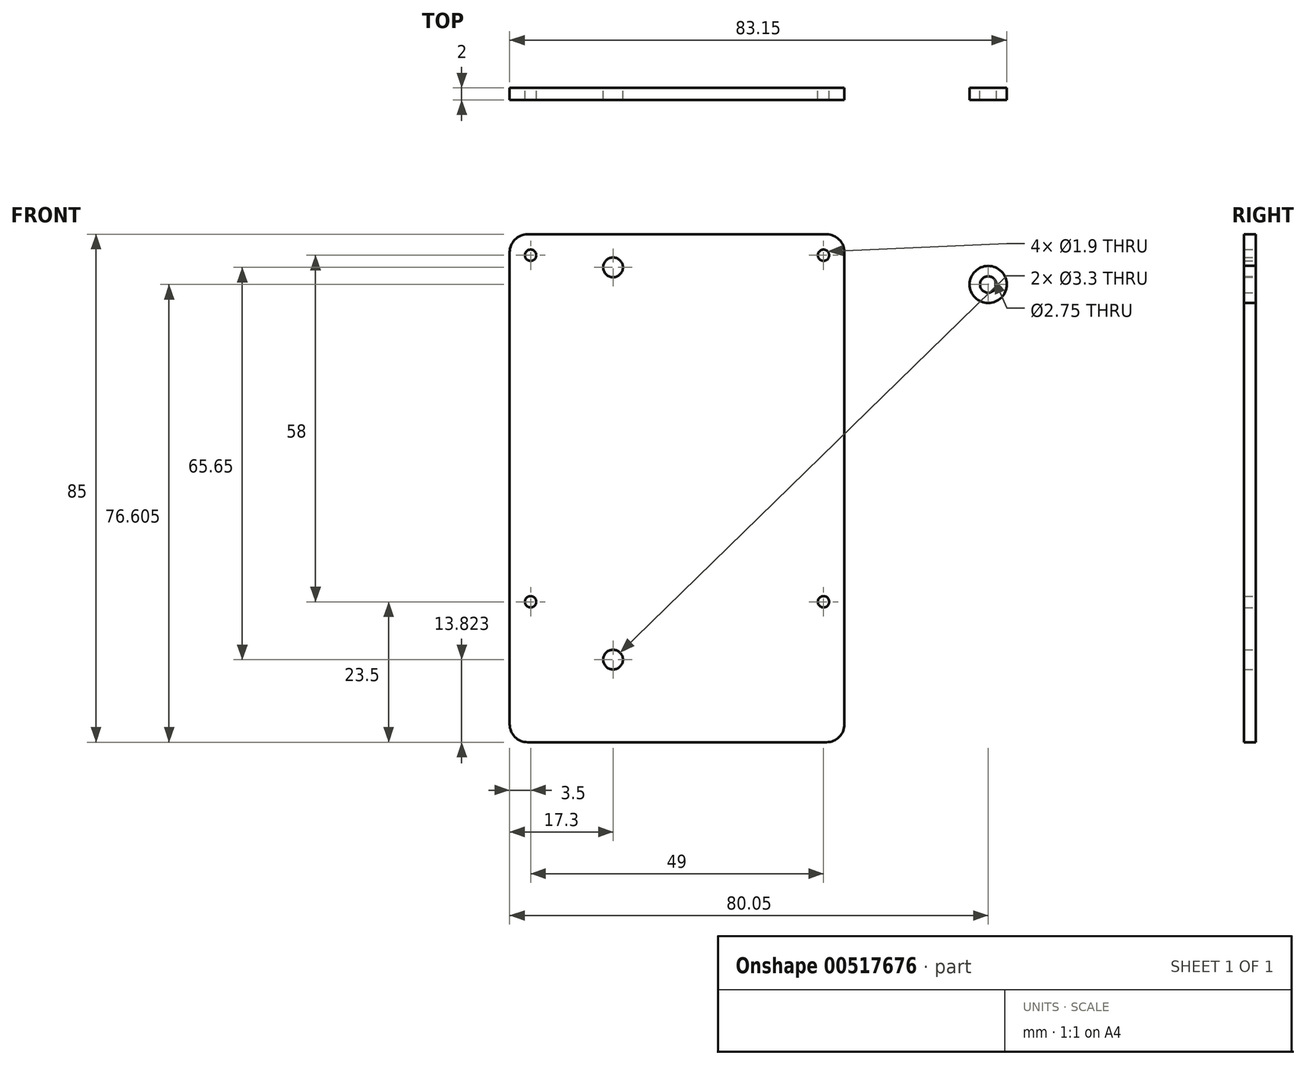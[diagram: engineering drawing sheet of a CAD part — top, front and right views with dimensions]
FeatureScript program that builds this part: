
annotation { "Feature Type Name" : "Feature", "Feature Type Description" : "" }
export const myFeature = defineFeature(function(context is Context, id is Id, definition is map)
    precondition{}
    {
        {
            var Q0;
            Q0=qCreatedBy(makeId("Front.planeOp"),FACE);
            var sketch = newSketch(context, id + "F0", { "sketchPlane" : qUnion([Q0])});
            skLineSegment(sketch, "E0.bottom", {"start": v(-25, 42.5) * mm, "end": v(25, 42.5) * mm});
            skLineSegment(sketch, "E0.top", {"start": v(-25, -42.5) * mm, "end": v(25, -42.5) * mm});
            skLineSegment(sketch, "E0.left", {"start": v(-28, 39.5) * mm, "end": v(-28, -39.5) * mm});
            skLineSegment(sketch, "E0.right", {"start": v(28, 39.5) * mm, "end": v(28, -39.5) * mm});
            skPoint(sketch, "E1", {"position": v(-28, 0) * mm});
            skPoint(sketch, "E2", {"position": v(0, 42.5) * mm});
            skCircle(sketch, "E3", {"center": v(-24.5, 39) * mm, "radius": 0.95 * mm});
            skCircle(sketch, "E4", {"center": v(24.5, 39) * mm, "radius": 0.95 * mm});
            skCircle(sketch, "E5", {"center": v(24.5, -19) * mm, "radius": 0.95 * mm});
            skCircle(sketch, "E6", {"center": v(-24.5, -19) * mm, "radius": 0.95 * mm});
            skCircle(sketch, "E7", {"center": v(-10.7, 36.97) * mm, "radius": 1.65 * mm});
            skCircle(sketch, "E8", {"center": v(-10.7, -28.68) * mm, "radius": 1.65 * mm});
            skPoint(sketch, "E9.visualSharp", {"position": v(28, 42.5) * mm});
            skArc(sketch, "E9.filletArc", {"start": v(28, 39.5) * mm, "mid": v(27.12, 41.62) * mm, "end": v(25, 42.5) * mm});
            skPoint(sketch, "E10.visualSharp", {"position": v(-28, 42.5) * mm});
            skArc(sketch, "E10.filletArc", {"start": v(-25, 42.5) * mm, "mid": v(-27.12, 41.62) * mm, "end": v(-28, 39.5) * mm});
            skPoint(sketch, "E11.visualSharp", {"position": v(-28, -42.5) * mm});
            skArc(sketch, "E11.filletArc", {"start": v(-28, -39.5) * mm, "mid": v(-27.12, -41.62) * mm, "end": v(-25, -42.5) * mm});
            skPoint(sketch, "E12.visualSharp", {"position": v(28, -42.5) * mm});
            skArc(sketch, "E12.filletArc", {"start": v(25, -42.5) * mm, "mid": v(27.12, -41.62) * mm, "end": v(28, -39.5) * mm});
            skCircle(sketch, "E13", {"center": v(52.05, 34.1) * mm, "radius": 3.1 * mm});
            skCircle(sketch, "E14", {"center": v(52.05, 34.1) * mm, "radius": 1.38 * mm});
            skSolve(sketch);
        }
        {
            var Q0;
            Q0 = qSketchRegion(id + "F0", true);
            extrude(context, id + "F1", {"entities" : qUnion([Q0]), "depth" : 2 * mm, "offsetDistance" : 25 * mm});
        }
    });
